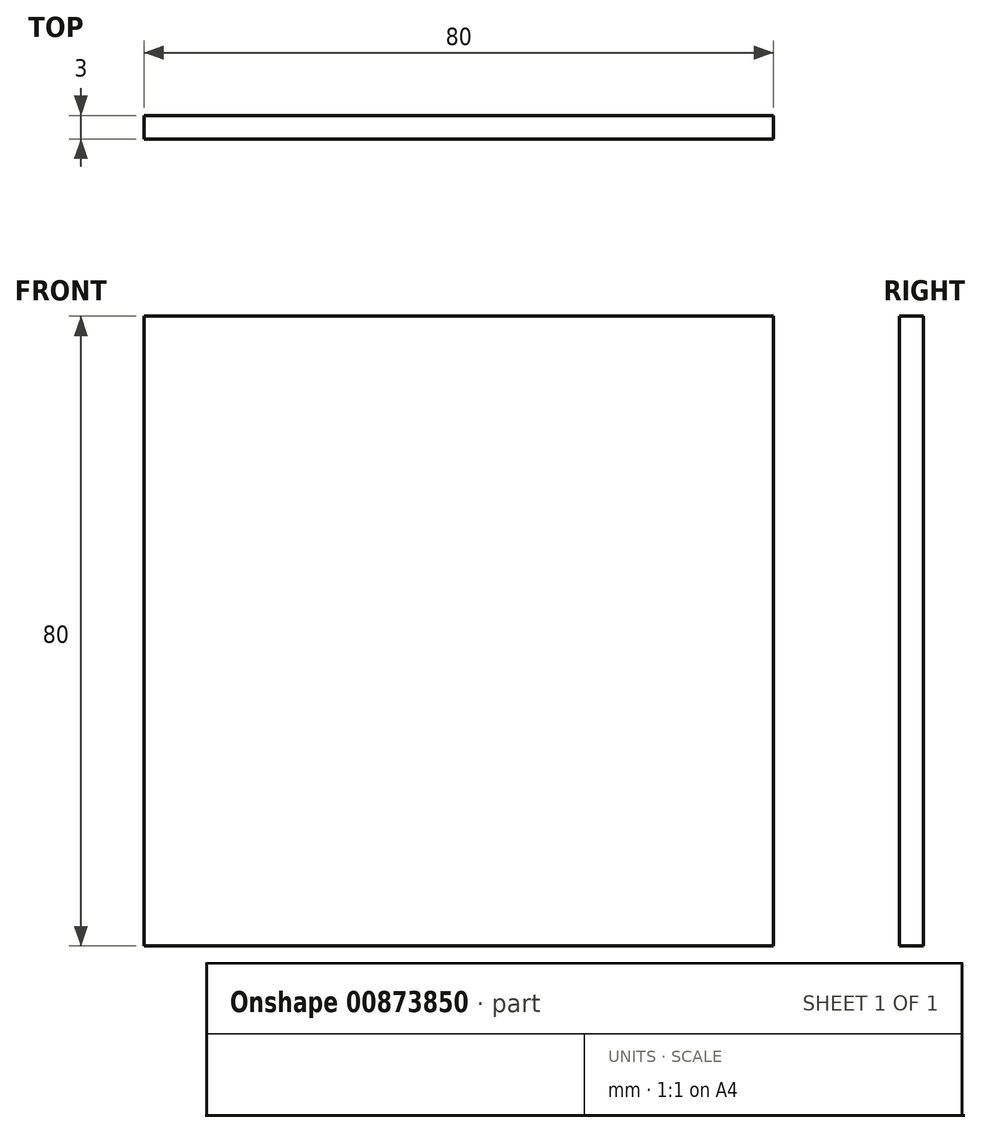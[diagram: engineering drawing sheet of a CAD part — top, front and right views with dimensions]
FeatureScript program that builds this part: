
annotation { "Feature Type Name" : "Feature", "Feature Type Description" : "" }
export const myFeature = defineFeature(function(context is Context, id is Id, definition is map)
    precondition{}
    {
        {
            var Q0;
            Q0=qCreatedBy(makeId("Front.planeOp"),FACE);
            var sketch = newSketch(context, id + "F0", { "sketchPlane" : qUnion([Q0])});
            skLineSegment(sketch, "E0.bottom", {"start": v(-40, 40) * mm, "end": v(40, 40) * mm});
            skLineSegment(sketch, "E0.top", {"start": v(-40, -40) * mm, "end": v(40, -40) * mm});
            skLineSegment(sketch, "E0.left", {"start": v(-40, 40) * mm, "end": v(-40, -40) * mm});
            skLineSegment(sketch, "E0.right", {"start": v(40, 40) * mm, "end": v(40, -40) * mm});
            skSolve(sketch);
        }
        {
            var Q0;
            Q0 = qSketchRegion(id + "F0", true);
            extrude(context, id + "F1", {"entities" : qUnion([Q0]), "depth" : 3 * mm, "offsetDistance" : 25 * mm});
        }
    });
